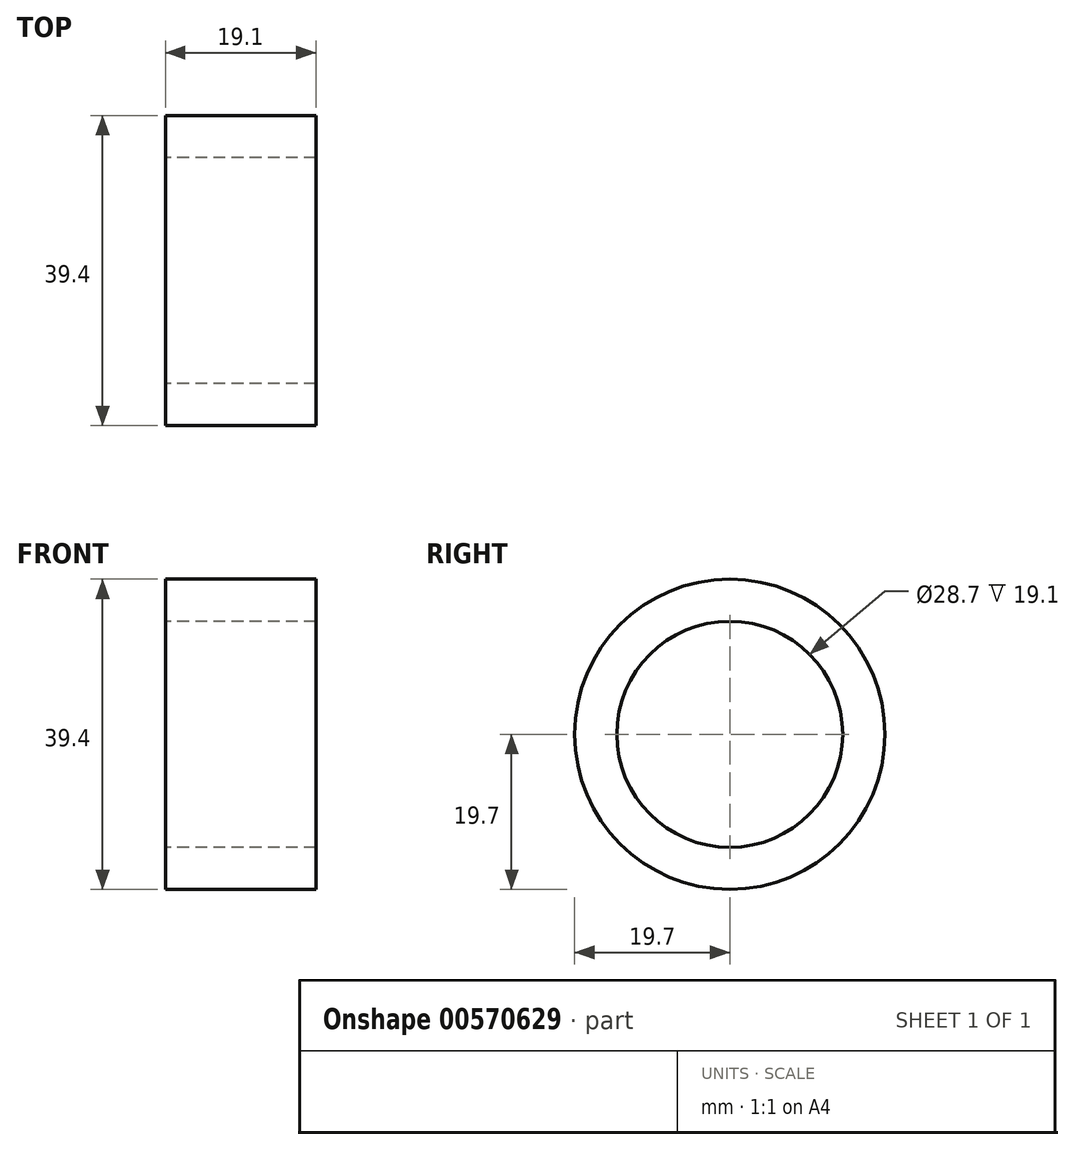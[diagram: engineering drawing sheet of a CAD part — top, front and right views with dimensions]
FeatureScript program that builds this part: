
annotation { "Feature Type Name" : "Feature", "Feature Type Description" : "" }
export const myFeature = defineFeature(function(context is Context, id is Id, definition is map)
    precondition{}
    {
        {
            var Q0;
            Q0=qCreatedBy(makeId("Top.planeOp"),FACE);
            var sketch = newSketch(context, id + "F0", { "sketchPlane" : qUnion([Q0])});
            skLineSegment(sketch, "E0", {"start": v(-65.15, 0) * mm, "end": v(0, 0) * mm, "construction": true});
            skLineSegment(sketch, "E1.bottom", {"start": v(-49.35, 19.7) * mm, "end": v(-30.25, 19.7) * mm});
            skLineSegment(sketch, "E1.top", {"start": v(-49.35, 14.35) * mm, "end": v(-30.25, 14.35) * mm});
            skLineSegment(sketch, "E1.left", {"start": v(-49.35, 19.7) * mm, "end": v(-49.35, 14.35) * mm});
            skLineSegment(sketch, "E1.right", {"start": v(-30.25, 19.7) * mm, "end": v(-30.25, 14.35) * mm});
            skLineSegment(sketch, "E2.MirrorCS", {"start": v(-49.35, -19.7) * mm, "end": v(-30.25, -19.7) * mm});
            skLineSegment(sketch, "E3.MirrorCS", {"start": v(-49.35, -14.35) * mm, "end": v(-30.25, -14.35) * mm});
            skLineSegment(sketch, "E4.MirrorCS", {"start": v(-30.25, -19.7) * mm, "end": v(-30.25, -14.35) * mm});
            skLineSegment(sketch, "E5.MirrorCS", {"start": v(-49.35, -19.7) * mm, "end": v(-49.35, -14.35) * mm});
            skSolve(sketch);
        }
        {
            var Q0;
            Q0=makeQuery(id+"F0.imprint","IMPRINT",FACE,{"disambiguationData":[TD([[makeQuery(id+"F0.imprint","IMPRINT",EDGE,{"derivedFrom":sQuery(id+"F0.wireOp",EDGE,"E1.bottom")}),-1.0]])]});
            var Q1;
            Q1=sQuery(id+"F0.wireOp",EDGE,"E0");
            revolve(context, id + "F1", {"entities" : qUnion([Q0]), "axis" : qUnion([Q1]), "revolveType" : RevolveType.FULL});
        }
    });
